# Revit family: Ciak 2.7
name_source: partatom
category: Lighting Fixtures
revit_build: Autodesk Revit 2017 (Build: 20160225_1515(x64)
units: mm (PartAtom-declared; Revit-internal decimal feet)

## family parameters
Cut with Voids When Loaded = Yes
Host = Face
Light Source = No
Part Type = Normal
Room Calculation Point = Yes
Round Connector Dimension = Use Diameter
Shared = No

## types (6) — shared parameters
Apparent Load Phase 1 = 5 W
Body = L&L_White aluminium
CRI = 90
Code = CK27001 B White; CK27001 N Black
Control system = -
Cutout dimensions = diam. 65 mm
Default Elevation = 1219 mm
Delivered lumen output = 303 lm (3000K, 32°)
Description = indoor recessed
Energy efficiency class = A A+ A++
Features = -
Geometry 1 = Ciak 2.0_Geometry 1
Geometry 2 = Ciak 2.0_mod : Ciak 2.7
Geometry 3 = Ciak 2.0_Geometry 3
Height mm = 30 mm  [stored 0.0984252 ft]
Height void = 30 mm  [stored 0.0984252 ft]
Horizontal rotation max = 350.00°
IP = 40
L1 = 17 mm
LED Colour = 3000K (also available: 2700K and 4000K - ref. URL Technical sheet)
Length mm = 61 mm  [stored 0.200131 ft]
Lens = L&L_Lens
Lumen output at source = 452 lm (3000K)
Manufacturer = L&L Luce&Light
Material = body and trim in aluminium
Model = Ciak 2.7
Mounting = recessed (ceiling, shelf, shop window)
No. and type of led = 1 high-intensity power LED
Notes = -
Power = 5W
Power cables = includes 1.5 m PVC cable FROR 2x0.35/0.35 diam. 3.5 m
Power supply = 24Vdc
Power supply unit = not included
Radius void = 33 mm
Trim = L&L_Black aluminium
URL = https://www.lucelight.it
URL Accessories and power supply units = https://www.lucelight.it
URL Catalogue = https://www.lucelight.it
URL DXF = https://www.lucelight.it
URL Description = https://www.lucelight.it
URL General code = https://www.lucelight.it
URL IES Photometric file = https://www.lucelight.it
URL Image = https://www.lucelight.it
URL Technical sheet = https://www.lucelight.it
Vertical rotation max = 70.00°
Voltage = 24 V
Weight kg = 0.15
Width mm = 61 mm  [stored 0.200131 ft]
Wiring = -

## per-type parameters (varying)
| type | Light Source | Optics |
| Ciak 2.7_J 65° (3000K 5W 24Vdc) | Light Source_2.7 : J65° | 65° |
| Ciak 2.7_L 32° (3000K 5W 24Vdc) | Light Source_2.7 : L32° | 32° |
| Ciak 2.7_M 17° (3000K 5W 24Vdc) | Light Source_2.7 : M17° | 17° |
| Ciak 2.7_P 19° (3000K 5W 24Vdc) | Light Source_2.7 : P19° | 19° |
| Ciak 2.7_S 11° (3000K 5W 24Vdc) | Light Source_2.7 : S11° | 11° |
| Ciak 2.7_W 13°x43° (3000K 5W 24Vdc) | Light Source_2.7 : W13°x43° | 13°x43° |

note: [stored X ft] marks values corroborated as IEEE doubles in the binary element streams (Revit-internal decimal feet)

## geometry (parser evidence)
native form markers: Blend x2, Sweep x16
no freeform markers — native parametric forms only
